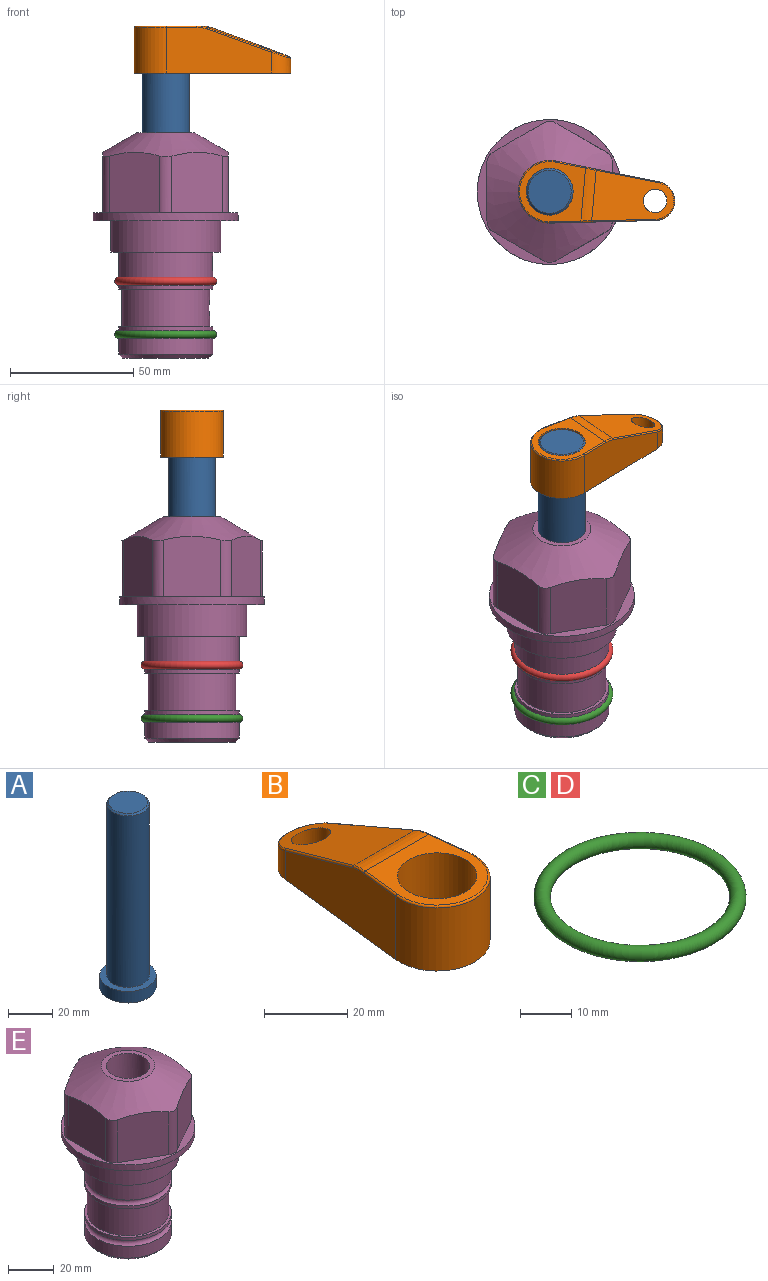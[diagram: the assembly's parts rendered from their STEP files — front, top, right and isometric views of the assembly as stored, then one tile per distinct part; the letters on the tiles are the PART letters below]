
ASSEMBLY  parts=5 mates=3
PART A: 6 faces, bbox 25.4x25.4x101.6 mm
  f0: plane 17.46x17.46mm, normal (0,0,1), area 239.5mm2, adj f5
  f1: plane 25.4x25.4mm, normal (0,0,-1), area 506.7mm2, adj f2
  f2: cylinder r=12.7mm len=25.4mm, axis (0,0,1), area 506.7mm2, adj f1,f3
  f3: plane 25.4x25.4mm, normal (0,0,1), area 221.7mm2, adj f2,f4
  f4: cylinder r=9.53mm len=94.46mm, axis (0,0,1), area 5653mm2, adj f3,f5
  f5: cone r=8.73mm half-angle=45deg, axis (0,0,-1), area 64.4mm2, adj f0,f4
PART B: 44 faces, bbox 27.5x64.5x19.1 mm
  f0: plane 2.3x0.95mm, normal (0,0,-1), area 1mm2, adj f25,f30,f34
  f1: plane 63.5x25.4mm, normal (0,0,-1), area 561.7mm2, adj f2,f3,f4,f5,f6,f7,f19,f20
  f2: cylinder r=12.7mm len=25.4mm, axis (0,0,-1), area 792.2mm2, adj f1,f3,f5,f13
  f3: plane 42.33x18.54mm, normal (0.99,0.11,0), area 647mm2, adj f1,f2,f4,f11,f12,f14
  f4: cylinder r=7.94mm len=15.78mm, axis (0,0,-1), area 158.6mm2, adj f1,f3,f5,f16
  f5: plane 42.33x18.54mm, normal (-0.99,0.11,0), area 647mm2, adj f1,f2,f4,f15,f17,f18
  f6: cylinder r=9.53mm len=19.05mm, axis (0,0,-1), area 1140.1mm2, adj f1,f8
  f7: cylinder r=4.76mm len=10.98mm, axis (0,0,-1), area 276.1mm2, adj f1,f9
  f8: plane 25.83x24.38mm, normal (0,0,1), area 262.2mm2, adj f6,f10,f11,f13,f15
  f9: plane 32.49x20.55mm, normal (0,0.34,0.94), area 489.9mm2, adj f7,f10,f14,f16,f18
  f10: cylinder r=12.7mm len=21.49mm, axis (-1,0,0), area 93.2mm2, adj f8,f9,f12,f17
  f11: cylinder r=0.51mm len=12.34mm, axis (0.11,-0.99,0), area 9.9mm2, adj f3,f8,f12,f13
  f12: bspline ~7.62x1.64mm, area 3.5mm2, adj f3,f10,f11,f14
  f13: torus R=12.19mm, axis (0,0,1), area 33.6mm2, adj f2,f8,f11,f15
  f14: cylinder r=0.51mm len=26.01mm, axis (0.1,-0.93,0.34), area 21.6mm2, adj f3,f9,f12,f16
  f15: cylinder r=0.51mm len=12.34mm, axis (0.11,0.99,0), area 9.9mm2, adj f5,f8,f13,f17
  f16: bspline ~15.78x7.05mm, area 15.7mm2, adj f4,f9,f14,f18
  f17: bspline ~7.62x1.64mm, area 3.5mm2, adj f5,f10,f15,f18
  f18: cylinder r=0.51mm len=26.01mm, axis (0.1,0.93,-0.34), area 21.6mm2, adj f5,f9,f16,f17
  f19: plane 21.6x14.29mm, normal (-0.99,-0.11,0), area 242.6mm2, adj f1,f26,f28,f34,f36,f38
  f20: plane 21.6x14.29mm, normal (0.99,-0.11,0), area 242.6mm2, adj f1,f27,f29,f37,f39,f41
  f21: cylinder r=12.7mm len=14.29mm, axis (0,0,-1), area 173.2mm2, adj f1,f26,f27,f30,f31,f33
  f22: cylinder r=7.94mm len=7.63mm, axis (0,0,-1), area 53.8mm2, adj f1,f28,f29,f42
  f23: plane 2.3x0.95mm, normal (0,0,-1), area 1mm2, adj f25,f33,f37
  f24: plane 17.94x12.32mm, normal (0,-0.34,-0.94), area 191.2mm2, adj f25,f38,f41,f42
  f25: cylinder r=9.53mm len=12.93mm, axis (-1,0,0), area 37.5mm2, adj f0,f23,f24,f31,f36,f39
  f26: cylinder r=1.59mm len=14.29mm, axis (0,0,-1), area 49mm2, adj f1,f19,f21,f32
  f27: cylinder r=1.59mm len=14.29mm, axis (0,0,-1), area 49mm2, adj f1,f20,f21,f35
  f28: cylinder r=1.59mm len=7.28mm, axis (0,0,-1), area 22.1mm2, adj f1,f19,f22,f40
  f29: cylinder r=1.59mm len=7.28mm, axis (0,0,-1), area 22.1mm2, adj f1,f20,f22,f43
  f30: torus R=14.29mm, axis (0,0,1), area 5.8mm2, adj f0,f21,f31,f32
  f31: bspline ~11.06x2.73mm, area 20.8mm2, adj f21,f25,f30,f33
  f32: sphere r=1.59mm, area 5.4mm2, adj f26,f30,f34
  f33: torus R=14.29mm, axis (0,0,1), area 5.8mm2, adj f21,f23,f31,f35
  f34: cylinder r=1.59mm len=1.68mm, axis (-0.11,0.99,0), area 2.4mm2, adj f0,f19,f32,f36
  f35: sphere r=1.59mm, area 5.4mm2, adj f27,f33,f37
  f36: bspline ~5.82x2.33mm, area 7.7mm2, adj f19,f25,f34,f38
  f37: cylinder r=1.59mm len=1.68mm, axis (0.11,0.99,0), area 2.4mm2, adj f20,f23,f35,f39
  f38: cylinder r=1.59mm len=18.33mm, axis (0.1,-0.93,0.34), area 46.7mm2, adj f19,f24,f36,f40
  f39: bspline ~5.82x2.33mm, area 7.7mm2, adj f20,f25,f37,f41
  f40: sphere r=1.59mm, area 3.6mm2, adj f28,f38,f42
  f41: cylinder r=1.59mm len=18.33mm, axis (0.1,0.93,-0.34), area 46.7mm2, adj f20,f24,f39,f43
  f42: bspline ~8.31x1.84mm, area 15.3mm2, adj f22,f24,f40,f43
  f43: sphere r=1.59mm, area 3.6mm2, adj f29,f41,f42
PART C: 1 faces, bbox 44.7x44.7x3.2 mm
  f0: torus R=19.05mm, axis (0,0,1), area 1193.9mm2
PART D: same geometry as C
PART E: 36 faces, bbox 58.7x58.7x91.2 mm
  f0: cylinder r=17.78mm len=35.56mm, axis (0,0,1), area 1670.8mm2, adj f23,f24,f31
  f1: cylinder r=19.05mm len=38.1mm, axis (0,0,1), area 1191.9mm2, adj f26,f27,f30
  f2: plane 58.66x58.66mm, normal (0,0,-1), area 1150.6mm2, adj f3,f28
  f3: cylinder r=29.33mm len=58.66mm, axis (0,0,-1), area 585.1mm2, adj f2,f4
  f4: plane 58.66x58.66mm, normal (0,0,1), area 475.9mm2, adj f3,f5,f6,f7,f8,f9,f10,f11
  f5: plane 24.5x20.32mm, normal (-0.5,0.87,0), area 562.8mm2, adj f4,f15,f16,f17
  f6: plane 24.5x20.32mm, normal (0.5,0.87,0), area 562.8mm2, adj f4,f14,f15,f17
  f7: plane 24.5x23.48mm, normal (1,0,0), area 562.8mm2, adj f4,f13,f14,f17
  f8: plane 24.5x20.32mm, normal (0.5,-0.87,0), area 562.8mm2, adj f4,f12,f13,f17
  f9: plane 24.5x20.32mm, normal (-0.5,-0.87,0), area 562.8mm2, adj f4,f11,f12,f17
  f10: plane 24.5x23.48mm, normal (-1,0,0), area 562.8mm2, adj f4,f11,f16,f17
  f11: cylinder r=5.08mm len=23.01mm, axis (0,0,-1), area 121.2mm2, adj f4,f9,f10,f17
  f12: cylinder r=5.08mm len=23.01mm, axis (0,0,-1), area 121.2mm2, adj f4,f8,f9,f17
  f13: cylinder r=5.08mm len=23.01mm, axis (0,0,-1), area 121.2mm2, adj f4,f7,f8,f17
  f14: cylinder r=5.08mm len=23.01mm, axis (0,0,-1), area 121.2mm2, adj f4,f6,f7,f17
  f15: cylinder r=5.08mm len=23.01mm, axis (0,0,-1), area 121.2mm2, adj f4,f5,f6,f17
  f16: cylinder r=5.08mm len=23.01mm, axis (0,0,-1), area 121.2mm2, adj f4,f5,f10,f17
  f17: cone r=11.73mm half-angle=60deg, axis (0,0,-1), area 2071.8mm2, adj f5,f6,f7,f8,f9,f10,f11,f12
  f18: plane 23.46x23.46mm, normal (0,0,1), area 147.4mm2, adj f17,f35
  f19: plane 34.93x34.93mm, normal (0,0,-1), area 958mm2, adj f29
  f20: cylinder r=19.05mm len=38.1mm, axis (0,0,1), area 760.1mm2, adj f21,f29
  f21: torus R=19.05mm, axis (0,0,1), area 565.3mm2, adj f20,f22
  f22: cylinder r=19.05mm len=38.1mm, axis (0,0,1), area 190mm2, adj f21,f23
  f23: plane 38.1x38.1mm, normal (0,0,1), area 146.9mm2, adj f0,f22
  f24: plane 38.1x38.1mm, normal (0,0,-1), area 146.9mm2, adj f0,f25
  f25: cylinder r=19.05mm len=38.1mm, axis (0,0,1), area 190mm2, adj f24,f26
  f26: torus R=19.05mm, axis (0,0,1), area 565.3mm2, adj f1,f25
  f27: plane 44.45x44.45mm, normal (0,0,-1), area 411.7mm2, adj f1,f28
  f28: cylinder r=22.23mm len=44.45mm, axis (0,0,1), area 1773.5mm2, adj f2,f27
  f29: cone r=19.05mm half-angle=45deg, axis (0,0,1), area 257.5mm2, adj f19,f20
  f30: cylinder r=3.17mm len=6.75mm, axis (-1,0,0), area 128mm2, adj f1,f33
  f31: cylinder r=3.17mm len=6.35mm, axis (-1,0,0), area 102.5mm2, adj f0,f33
  f32: plane 25.4x25.4mm, normal (0,0,1), area 506.7mm2, adj f33
  f33: cylinder r=12.7mm len=66.42mm, axis (0,0,-1), area 5236.2mm2, adj f30,f31,f32,f34
  f34: cone r=9.53mm half-angle=30deg, axis (0,0,-1), area 443.4mm2, adj f33,f35
  f35: cylinder r=9.53mm len=19.05mm, axis (0,0,-1), area 849mm2, adj f18,f34
PLACE A rot(axis=(0,0,-1),5deg) t=(0,0,5.18)mm
PLACE B rot(axis=(0,0,-1),95deg) t=(0,0,59.79)mm
PLACE C t=(0,0,-21.59)mm
PLACE D at identity
PLACE E at identity fixed
MATE fastened C.f0 <-> E.f0  axis (0,0,1) through (0,0,-46.1)mm
MATE cylindrical A.f2 <-> E.f0  axis (0,0,1) through (0,0,30.81)mm
MATE fastened B.f2 <-> A.f2  axis (0,0,1) through (0,0,78.84)mm
